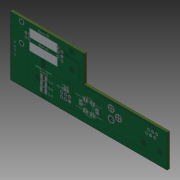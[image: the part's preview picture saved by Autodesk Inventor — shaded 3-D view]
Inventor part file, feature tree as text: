
AUTODESK INVENTOR PART (.ipt)
format: ipt  version: 2014 SP1 (Build 180222100, 222)  size: 103,424 bytes
history: native  units: mm
features: extrude x1, sketch x1
ambient origin geometry x8: Origin, YZ Plane, XZ Plane, XY Plane, X Axis, Y Axis, Z Axis, Center Point
bodies: Solid1 (feature_tree)
feature tree (2):
  extrude  "Extrusion1"  Depth=17.0mm
  sketch  "Sketch1"  dims[d0=47.0mm d1=17.0mm d2=100.0mm d3=21.0mm d4=10.5mm d5=50.0mm d6=1.6mm d7=0.0mm]
